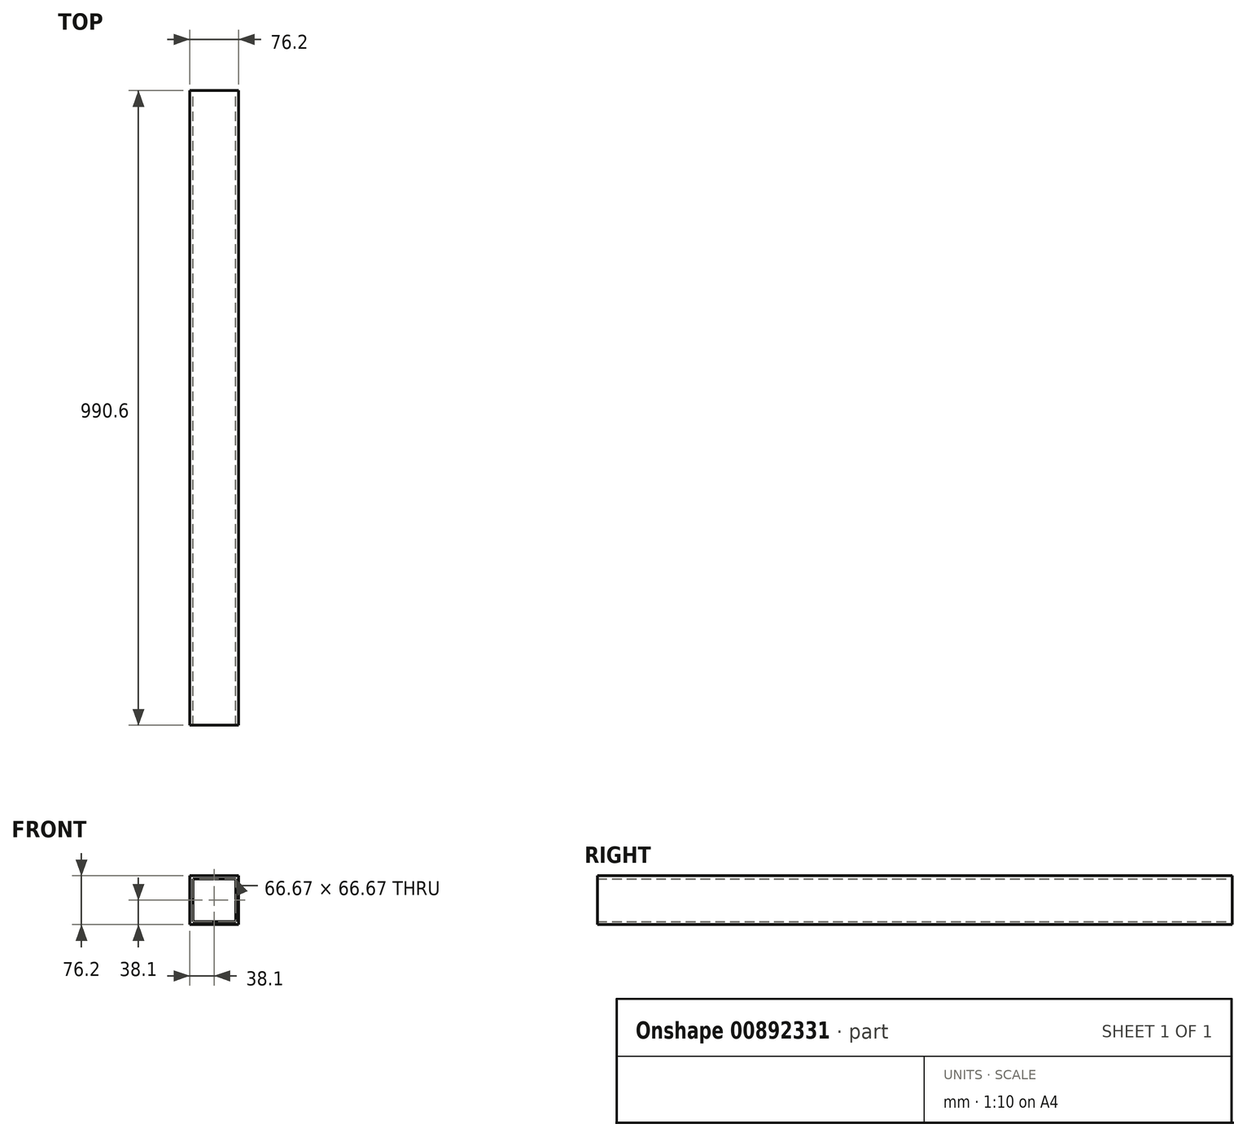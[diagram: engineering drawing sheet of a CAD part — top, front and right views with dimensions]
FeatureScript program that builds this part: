
annotation { "Feature Type Name" : "Feature", "Feature Type Description" : "" }
export const myFeature = defineFeature(function(context is Context, id is Id, definition is map)
    precondition{}
    {
        {
            var Q0;
            Q0=qCreatedBy(makeId("Front.planeOp"),FACE);
            var sketch = newSketch(context, id + "F0", { "sketchPlane" : qUnion([Q0])});
            skLineSegment(sketch, "E0.bottom", {"start": v(38.1, 38.1) * mm, "end": v(-38.1, 38.1) * mm});
            skLineSegment(sketch, "E0.top", {"start": v(38.1, -38.1) * mm, "end": v(-38.1, -38.1) * mm});
            skLineSegment(sketch, "E0.left", {"start": v(38.1, 38.1) * mm, "end": v(38.1, -38.1) * mm});
            skLineSegment(sketch, "E0.right", {"start": v(-38.1, 38.1) * mm, "end": v(-38.1, -38.1) * mm});
            skPoint(sketch, "E0.middle", {"position": v(0, 0) * mm});
            skLineSegment(sketch, "E1.bottom", {"start": v(-33.34, 33.34) * mm, "end": v(33.34, 33.34) * mm});
            skLineSegment(sketch, "E1.top", {"start": v(-33.34, -33.34) * mm, "end": v(33.34, -33.34) * mm});
            skLineSegment(sketch, "E1.left", {"start": v(-33.34, 33.34) * mm, "end": v(-33.34, -33.34) * mm});
            skLineSegment(sketch, "E1.right", {"start": v(33.34, 33.34) * mm, "end": v(33.34, -33.34) * mm});
            skSolve(sketch);
        }
        {
            var Q0;
            Q0 = qSketchRegion(id + "F0", true);
            extrude(context, id + "F1", {"entities" : qUnion([Q0]), "depth" : 990.6 * mm, "offsetDistance" : 25.4 * mm});
        }
    });
